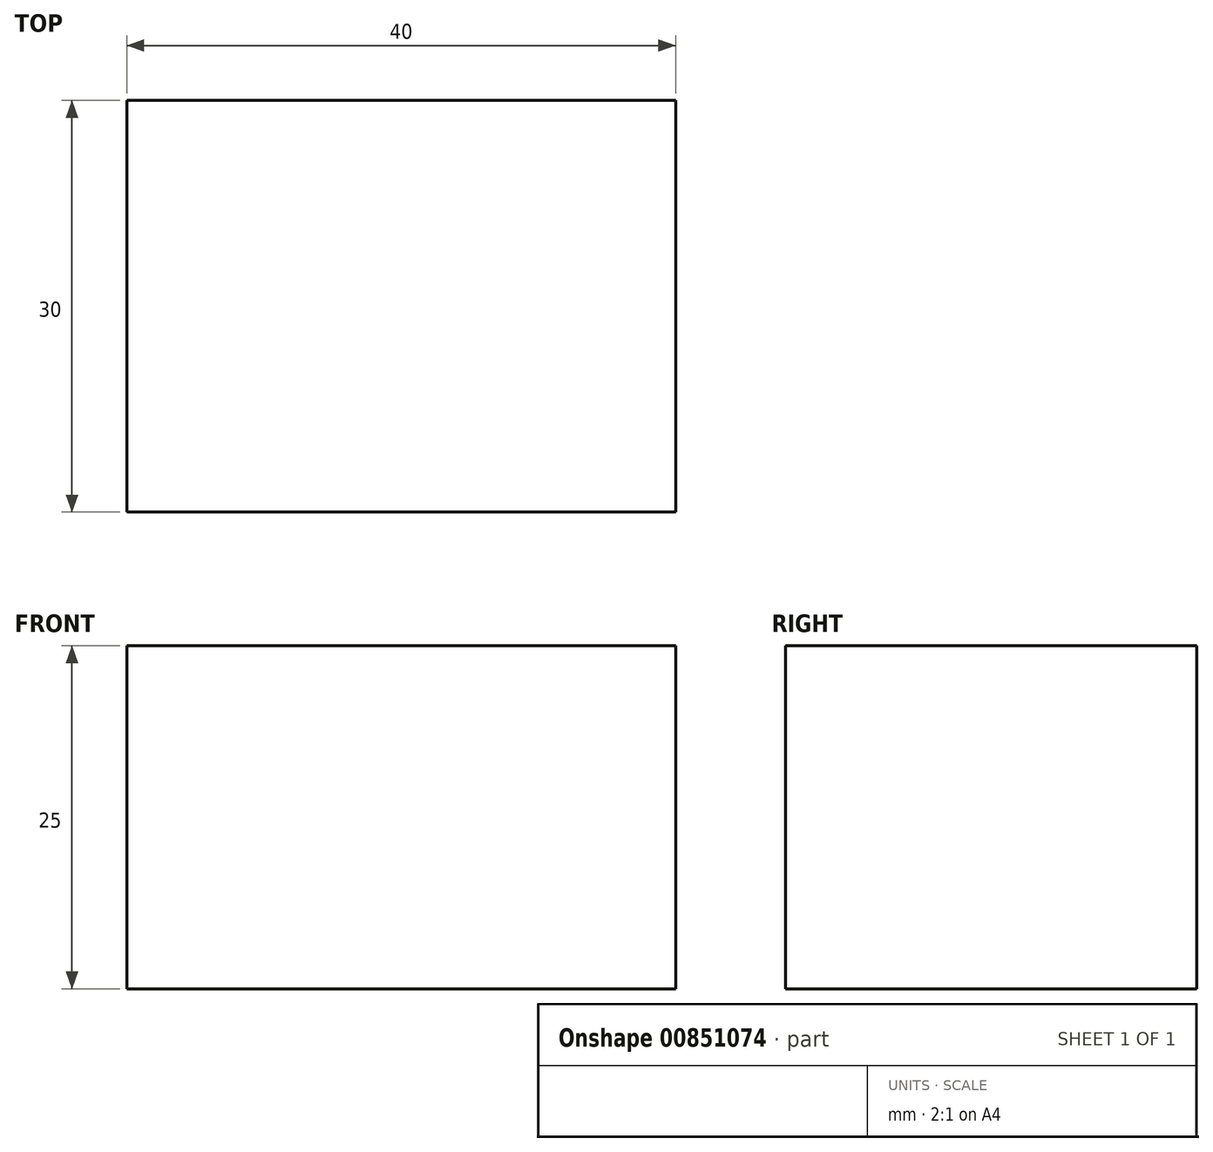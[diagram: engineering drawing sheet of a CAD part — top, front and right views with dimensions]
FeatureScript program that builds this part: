
annotation { "Feature Type Name" : "Feature", "Feature Type Description" : "" }
export const myFeature = defineFeature(function(context is Context, id is Id, definition is map)
    precondition{}
    {
        {
            var Q0;
            Q0=qCreatedBy(makeId("Top.planeOp"),FACE);
            var sketch = newSketch(context, id + "F0", { "sketchPlane" : qUnion([Q0])});
            skLineSegment(sketch, "E0.bottom", {"start": v(-20, -15) * mm, "end": v(20, -15) * mm});
            skLineSegment(sketch, "E0.top", {"start": v(-20, 15) * mm, "end": v(20, 15) * mm});
            skLineSegment(sketch, "E0.left", {"start": v(-20, -15) * mm, "end": v(-20, 15) * mm});
            skLineSegment(sketch, "E0.right", {"start": v(20, -15) * mm, "end": v(20, 15) * mm});
            skLineSegment(sketch, "E1", {"start": v(-20, -15) * mm, "end": v(20, 15) * mm, "construction": true});
            skSolve(sketch);
        }
        {
            var Q0;
            Q0 = qSketchRegion(id + "F0", true);
            extrude(context, id + "F1", {"entities" : qUnion([Q0]), "depth" : 25 * mm, "offsetDistance" : 25 * mm});
        }
    });
